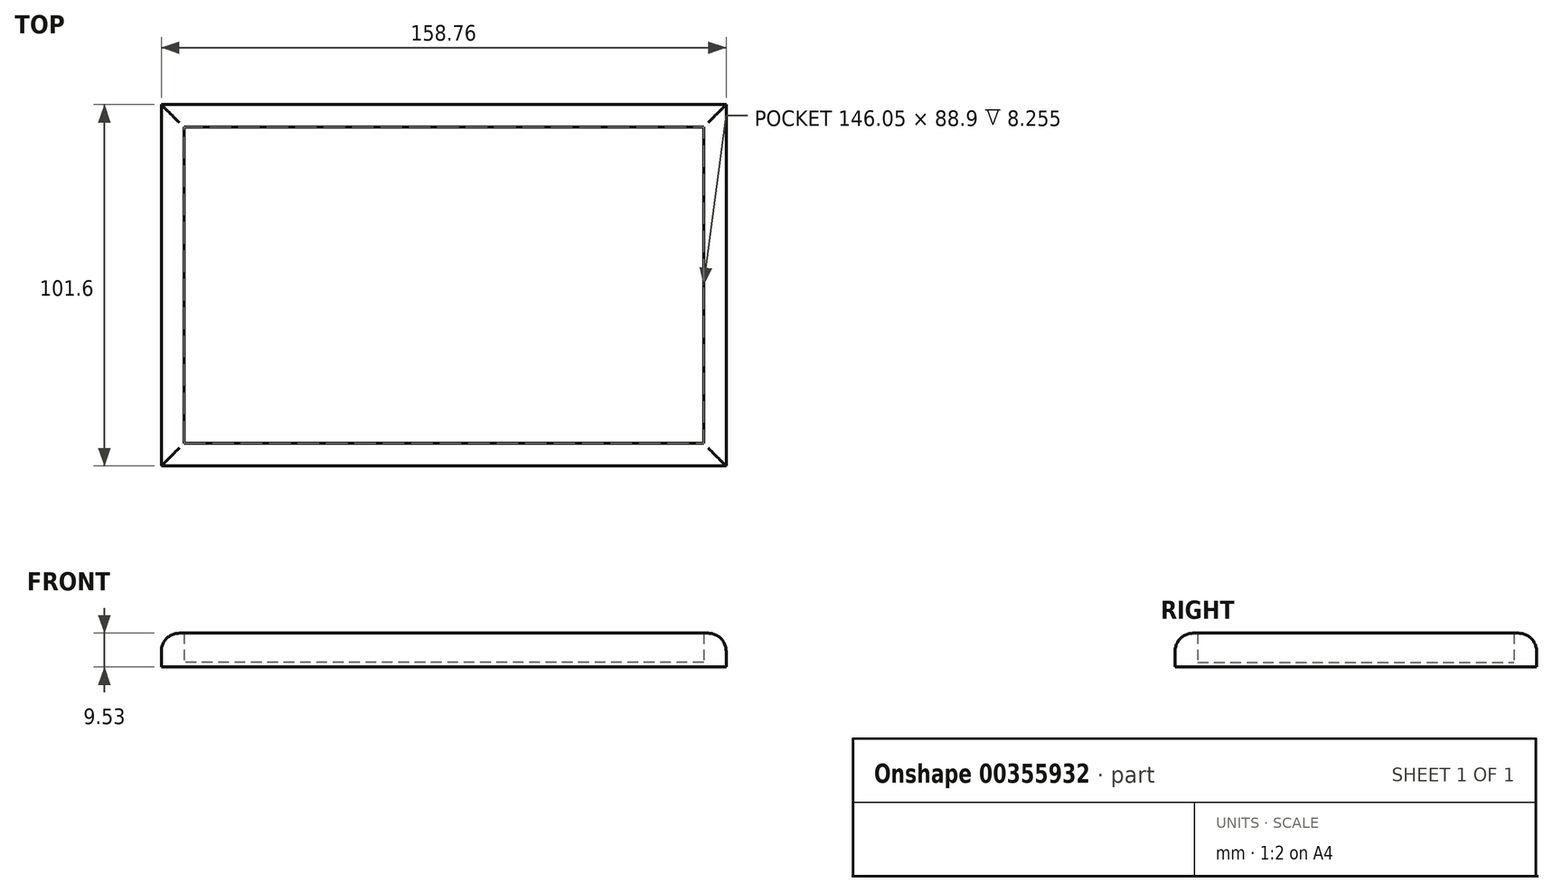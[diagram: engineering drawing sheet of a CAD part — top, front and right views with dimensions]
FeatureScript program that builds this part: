
annotation { "Feature Type Name" : "Feature", "Feature Type Description" : "" }
export const myFeature = defineFeature(function(context is Context, id is Id, definition is map)
    precondition{}
    {
        {
            var Q0;
            Q0=qCreatedBy(makeId("Top.planeOp"),FACE);
            var sketch = newSketch(context, id + "F0", { "sketchPlane" : qUnion([Q0])});
            skPoint(sketch, "E0.middle", {"position": v(0, 0) * mm});
            skLineSegment(sketch, "E1.0", {"start": v(79.38, 50.8) * mm, "end": v(-79.38, 50.8) * mm});
            skLineSegment(sketch, "E1.1", {"start": v(79.38, -50.8) * mm, "end": v(79.38, 50.8) * mm});
            skLineSegment(sketch, "E1.2", {"start": v(79.38, -50.8) * mm, "end": v(-79.38, -50.8) * mm});
            skLineSegment(sketch, "E1.3", {"start": v(-79.38, -50.8) * mm, "end": v(-79.38, 50.8) * mm});
            skLineSegment(sketch, "E2.0", {"start": v(-73.03, -44.45) * mm, "end": v(-73.03, 44.45) * mm});
            skLineSegment(sketch, "E2.1", {"start": v(73.03, -44.45) * mm, "end": v(-73.03, -44.45) * mm});
            skLineSegment(sketch, "E2.2", {"start": v(73.03, -44.45) * mm, "end": v(73.03, 44.45) * mm});
            skLineSegment(sketch, "E2.3", {"start": v(73.03, 44.45) * mm, "end": v(-73.03, 44.45) * mm});
            skPoint(sketch, "E0.right.end.orphan", {"position": v(-76.2, 47.62) * mm});
            skPoint(sketch, "E0.bottom.end.orphan", {"position": v(-76.2, -47.63) * mm});
            skPoint(sketch, "E0.left.end.orphan", {"position": v(76.2, 47.63) * mm});
            skPoint(sketch, "E0.left.start.orphan", {"position": v(76.2, -47.62) * mm});
            skSolve(sketch);
        }
        {
            var Q0;
            Q0=qSketchRegion(id+"F0",true);
            extrude(context, id + "F1", {"entities" : qUnion([Q0]), "depth" : 9.52 * mm});
        }
        {
            var Q0;
            Q0=makeQuery(id+"F1.opExtrude","CAP_EDGE",EDGE,{"disambiguationData":[OSD([sQuery(id+"F0.wireOp",EDGE,"E1.3")])],"isStart":false});
            var Q1;
            Q1=makeQuery(id+"F1.opExtrude","CAP_EDGE",EDGE,{"disambiguationData":[OSD([sQuery(id+"F0.wireOp",EDGE,"E1.2")])],"isStart":false});
            var Q2;
            Q2=makeQuery(id+"F1.opExtrude","CAP_EDGE",EDGE,{"disambiguationData":[OSD([sQuery(id+"F0.wireOp",EDGE,"E1.1")])],"isStart":false});
            var Q3;
            Q3=makeQuery(id+"F1.opExtrude","CAP_EDGE",EDGE,{"disambiguationData":[OSD([sQuery(id+"F0.wireOp",EDGE,"E1.0")])],"isStart":false});
            fillet(context, id + "F2", {"entities" : qUnion([Q0, Q1, Q2, Q3]), "radius" : 5.08 * mm, "tangentPropagation" : true, "allowEdgeOverflow" : false});
        }
        {
            var Q0;
            Q0=makeQuery(id+"F0.imprint","IMPRINT",FACE,{"disambiguationData":[TD([[makeQuery(id+"F0.imprint","IMPRINT",EDGE,{"derivedFrom":sQuery(id+"F0.wireOp",EDGE,"E2.0")}),-1.0]])]});
            extrude(context, id + "F3", {"entities" : qUnion([Q0]), "operationType" : NewBodyOperationType.ADD, "depth" : 1.27 * mm});
        }
    });
